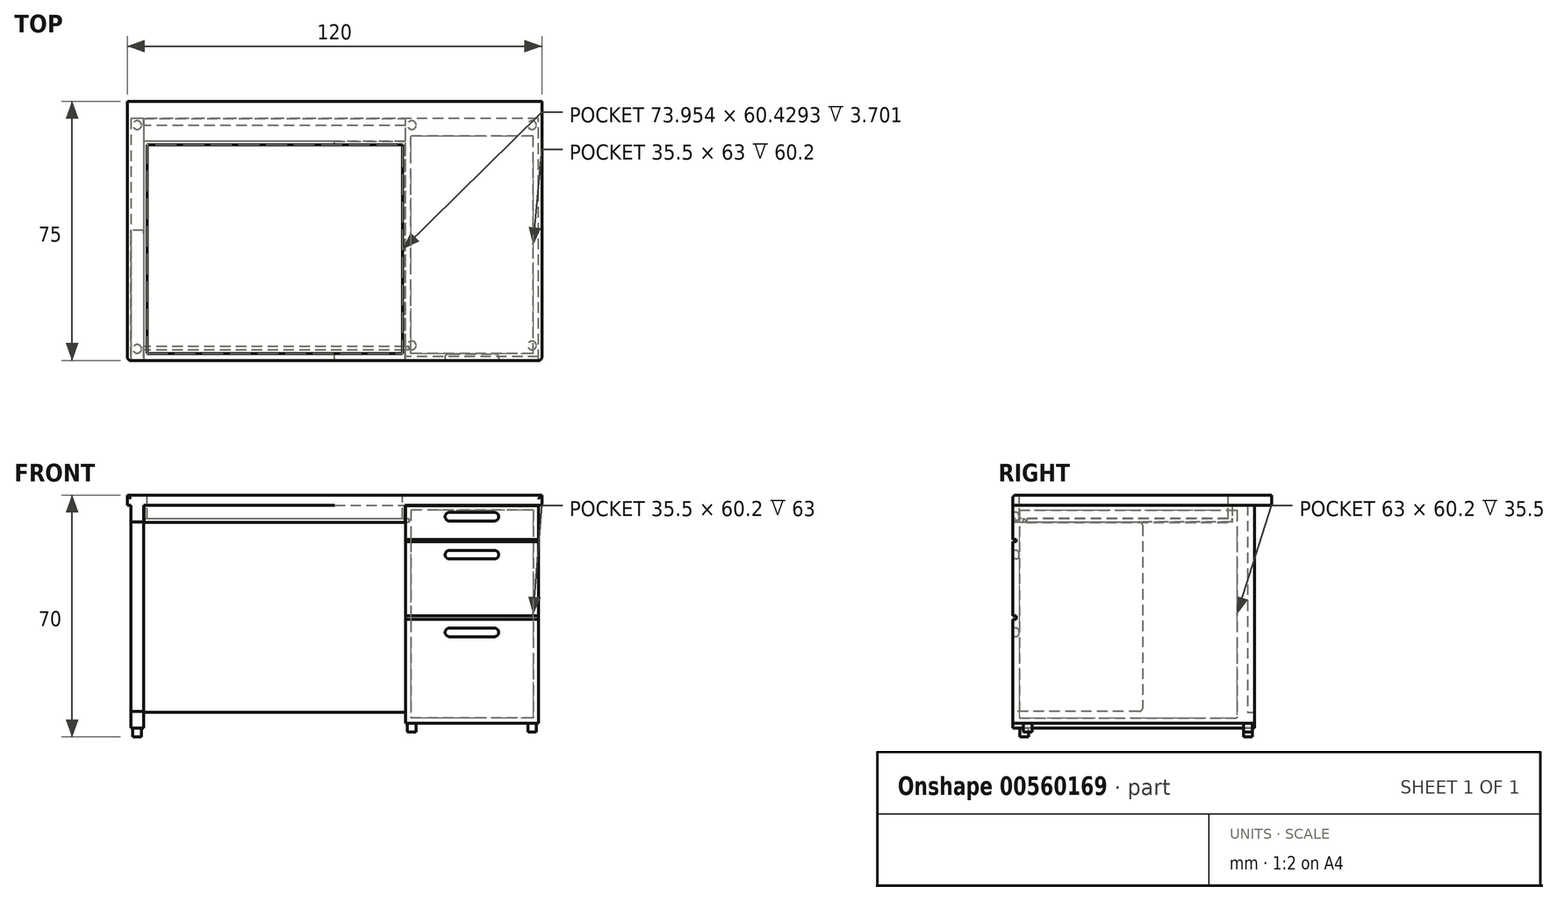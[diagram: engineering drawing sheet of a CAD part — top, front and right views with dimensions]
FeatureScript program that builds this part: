
annotation { "Feature Type Name" : "Feature", "Feature Type Description" : "" }
export const myFeature = defineFeature(function(context is Context, id is Id, definition is map)
    precondition{}
    {
        {
            var Q0;
            Q0=qCreatedBy(makeId("Top.planeOp"),FACE);
            var sketch = newSketch(context, id + "F0", { "sketchPlane" : qUnion([Q0])});
            skLineSegment(sketch, "E0.top", {"start": v(-60, -35) * mm, "end": v(60, -35) * mm});
            skPoint(sketch, "E0.middle", {"position": v(0, 0) * mm});
            skLineSegment(sketch, "E1", {"start": v(-60, 40) * mm, "end": v(60, 40) * mm});
            skLineSegment(sketch, "E2", {"start": v(-60, -35) * mm, "end": v(-60, 40) * mm});
            skLineSegment(sketch, "E3", {"start": v(60, 40) * mm, "end": v(60, -35) * mm});
            skSolve(sketch);
        }
        {
            var Q0;
            Q0 = qSketchRegion(id + "F0", true);
            extrude(context, id + "F1", {"entities" : qUnion([Q0]), "depth" : 2.9 * mm, "offsetDistance" : 25 * mm});
        }
        {
            var Q0;
            Q0=makeQuery(id+"F1.opExtrude","CAP_EDGE",EDGE,{"disambiguationData":[OSD([sQuery(id+"F0.wireOp",EDGE,"E0.bottom")])],"isStart":false});
            var Q1;
            Q1=makeQuery(id+"F1.opExtrude","CAP_EDGE",EDGE,{"disambiguationData":[OSD([sQuery(id+"F0.wireOp",EDGE,"E0.right")])],"isStart":false});
            var Q2;
            Q2=makeQuery(id+"F1.opExtrude","CAP_EDGE",EDGE,{"disambiguationData":[OSD([sQuery(id+"F0.wireOp",EDGE,"E0.left")])],"isStart":false});
            var Q3;
            Q3=makeQuery(id+"F1.opExtrude","CAP_EDGE",EDGE,{"disambiguationData":[OSD([sQuery(id+"F0.wireOp",EDGE,"E0.top")])],"isStart":false});
            var Q4;
            Q4=makeQuery(id+"F1.opExtrude","SWEPT_EDGE",EDGE,{"disambiguationData":[OSD([sQuery(id+"F0.wireOp",EDGE,"E0.top"),sQuery(id+"F0.wireOp",EDGE,"E0.left")])]});
            var Q5;
            Q5=makeQuery(id+"F1.opExtrude","SWEPT_EDGE",EDGE,{"disambiguationData":[OSD([sQuery(id+"F0.wireOp",EDGE,"E0.bottom"),sQuery(id+"F0.wireOp",EDGE,"E0.left")])]});
            var Q6;
            Q6=makeQuery(id+"F1.opExtrude","SWEPT_EDGE",EDGE,{"disambiguationData":[OSD([sQuery(id+"F0.wireOp",EDGE,"E0.bottom"),sQuery(id+"F0.wireOp",EDGE,"E0.right")])]});
            var Q7;
            Q7=makeQuery(id+"F1.opExtrude","SWEPT_EDGE",EDGE,{"disambiguationData":[OSD([sQuery(id+"F0.wireOp",EDGE,"E0.top"),sQuery(id+"F0.wireOp",EDGE,"E0.right")])]});
            fillet(context, id + "F2", {"entities" : qUnion([Q0, Q1, Q2, Q3, Q4, Q5, Q6, Q7]), "radius" : 1 * mm, "tangentPropagation" : true, "allowEdgeOverflow" : false});
        }
        {
            var Q0;
            Q0=qCreatedBy(makeId("Top.planeOp"),FACE);
            var sketch = newSketch(context, id + "F3", { "sketchPlane" : qUnion([Q0])});
            skLineSegment(sketch, "E4", {"start": v(-55.3, 0) * mm, "end": v(-55.3, -35) * mm});
            skLineSegment(sketch, "E5", {"start": v(-55.3, 0) * mm, "end": v(-55.3, 35) * mm});
            skLineSegment(sketch, "E6", {"start": v(-55.3, 35) * mm, "end": v(-59, 35) * mm});
            skLineSegment(sketch, "E7", {"start": v(-59, 35) * mm, "end": v(-59, -35) * mm});
            skLineSegment(sketch, "E8", {"start": v(-59, -35) * mm, "end": v(-55.3, -35) * mm});
            skPoint(sketch, "E9", {"position": v(-59, 0) * mm});
            skSolve(sketch);
        }
        {
            var Q0;
            Q0 = qSketchRegion(id + "F3", true);
            extrude(context, id + "F4", {"entities" : qUnion([Q0]), "operationType" : NewBodyOperationType.ADD, "oppositeDirection" : true, "depth" : 64.6 * mm, "offsetDistance" : 25 * mm});
        }
        {
            var Q0;
            Q0=qCreatedBy(makeId("Front.planeOp"),FACE);
            cPlane(context, id + "F5", {"entities" : qUnion([Q0]), "cplaneType" : CPlaneType.OFFSET, "offset" : 35 * mm, "oppositeDirection" : true, "width" : 150 * mm, "height" : 150 * mm});
        }
        {
            var Q0;
            Q0=qCreatedBy(id+"F5.planeOp",FACE);
            var sketch = newSketch(context, id + "F6", { "sketchPlane" : qUnion([Q0])});
            skLineSegment(sketch, "E10", {"start": v(0, 0) * mm, "end": v(-55.3, 0) * mm});
            skLineSegment(sketch, "E11.bottom", {"start": v(-55.3, 0) * mm, "end": v(20.5, 0) * mm});
            skLineSegment(sketch, "E11.top", {"start": v(-55.3, -60) * mm, "end": v(20.5, -60) * mm});
            skLineSegment(sketch, "E11.left", {"start": v(-55.3, 0) * mm, "end": v(-55.3, -60) * mm});
            skLineSegment(sketch, "E11.right", {"start": v(20.5, 0) * mm, "end": v(20.5, -60) * mm});
            skSolve(sketch);
        }
        {
            var Q0;
            Q0 = qSketchRegion(id + "F6", true);
            extrude(context, id + "F7", {"entities" : qUnion([Q0]), "operationType" : NewBodyOperationType.ADD, "depth" : 2 * mm, "offsetDistance" : 25 * mm});
        }
        {
            var Q0;
            Q0=makeQuery(id+"F7.boolean.opBoolean","MERGE",FACE,{"derivedFrom":[makeQuery(id+"F4.boolean.opBoolean","MERGE",FACE,{"derivedFrom":[makeQuery(id+"F1.opExtrude","SWEPT_FACE",FACE,{"disambiguationData":[OSD([sQuery(id+"F0.wireOp",EDGE,"E0.bottom")])]}),makeQuery(id+"F4.opExtrude","SWEPT_FACE",FACE,{"disambiguationData":[OSD([sQuery(id+"F3.wireOp",EDGE,"E6")])]})]}),makeQuery(id+"F7.opExtrude","CAP_FACE",FACE,{"disambiguationData":[OSD([sQuery(id+"F6.wireOp",EDGE,"E11.bottom"),sQuery(id+"F6.wireOp",EDGE,"E11.top"),sQuery(id+"F6.wireOp",EDGE,"E11.left"),sQuery(id+"F6.wireOp",EDGE,"E11.right")])],"isStart":true})]});
            var sketch = newSketch(context, id + "F8", { "sketchPlane" : qUnion([Q0])});
            skLineSegment(sketch, "E12", {"start": v(-20.5, 0) * mm, "end": v(-20.5, -9.9) * mm});
            skLineSegment(sketch, "E13", {"start": v(-20.5, -9.9) * mm, "end": v(-20.5, -31.4) * mm});
            skLineSegment(sketch, "E14", {"start": v(-20.5, -31.4) * mm, "end": v(-20.5, -63.2) * mm});
            skLineSegment(sketch, "E15.bottom", {"start": v(-20.5, 0) * mm, "end": v(-59, 0) * mm});
            skLineSegment(sketch, "E15.right", {"start": v(-59, 0) * mm, "end": v(-59, -9.9) * mm});
            skLineSegment(sketch, "E16.left", {"start": v(-59, -9.9) * mm, "end": v(-59, -31.4) * mm});
            skLineSegment(sketch, "E17.top", {"start": v(-59, -63.2) * mm, "end": v(-20.5, -63.2) * mm});
            skLineSegment(sketch, "E17.left", {"start": v(-59, -31.4) * mm, "end": v(-59, -63.2) * mm});
            skLineSegment(sketch, "E18.bottom", {"start": v(-57.5, -1.5) * mm, "end": v(-22, -1.5) * mm});
            skLineSegment(sketch, "E18.top", {"start": v(-57.5, -61.7) * mm, "end": v(-22, -61.7) * mm});
            skLineSegment(sketch, "E18.left", {"start": v(-57.5, -1.5) * mm, "end": v(-57.5, -61.7) * mm});
            skLineSegment(sketch, "E18.right", {"start": v(-22, -1.5) * mm, "end": v(-22, -61.7) * mm});
            skSolve(sketch);
        }
        {
            var Q0;
            Q0=makeQuery(id+"F4.opExtrude","SWEPT_FACE",FACE,{"disambiguationData":[OSD([sQuery(id+"F3.wireOp",EDGE,"E7")])]});
            var sketch = newSketch(context, id + "F9", { "sketchPlane" : qUnion([Q0])});
            skLineSegment(sketch, "E19", {"start": v(35, -4.9) * mm, "end": v(-2.66, -4.9) * mm});
            skLineSegment(sketch, "E20", {"start": v(-2.66, -4.9) * mm, "end": v(-2.66, -59.7) * mm});
            skLineSegment(sketch, "E21", {"start": v(-2.66, -59.7) * mm, "end": v(35, -59.7) * mm});
            skLineSegment(sketch, "E22", {"start": v(35, -59.7) * mm, "end": v(35, -4.9) * mm});
            skSolve(sketch);
        }
        {
            var Q0;
            Q0 = qSketchRegion(id + "F9", true);
            extrude(context, id + "F10", {"entities" : qUnion([Q0]), "operationType" : NewBodyOperationType.REMOVE, "oppositeDirection" : true, "depth" : 25 * mm, "offsetDistance" : 25 * mm});
        }
        {
            var Q0;
            Q0=makeQuery(id+"F10.boolean.opBoolean","COPY",EDGE,{"derivedFrom":makeQuery(id+"F10.opExtrude","SWEPT_EDGE",EDGE,{"disambiguationData":[OSD([sQuery(id+"F9.wireOp",EDGE,"E19"),sQuery(id+"F9.wireOp",EDGE,"E20")])]})});
            var Q1;
            Q1=makeQuery(id+"F10.boolean.opBoolean","COPY",EDGE,{"derivedFrom":makeQuery(id+"F10.opExtrude","SWEPT_EDGE",EDGE,{"disambiguationData":[OSD([sQuery(id+"F9.wireOp",EDGE,"E20"),sQuery(id+"F9.wireOp",EDGE,"E21")])]})});
            var Q2;
            Q2=makeQuery(id+"F10.boolean.opBoolean","COPY",EDGE,{"derivedFrom":makeQuery(id+"F10.opExtrude","SWEPT_EDGE",EDGE,{"disambiguationData":[OSD([sQuery(id+"F3.wireOp",EDGE,"E7"),sQuery(id+"F3.wireOp",EDGE,"E8"),sQuery(id+"F9.wireOp",EDGE,"E19"),sQuery(id+"F9.wireOp",EDGE,"E22")])]})});
            var Q3;
            Q3=makeQuery(id+"F10.boolean.opBoolean","COPY",EDGE,{"derivedFrom":makeQuery(id+"F10.opExtrude","SWEPT_EDGE",EDGE,{"disambiguationData":[OSD([sQuery(id+"F3.wireOp",EDGE,"E7"),sQuery(id+"F3.wireOp",EDGE,"E8"),sQuery(id+"F9.wireOp",EDGE,"E21"),sQuery(id+"F9.wireOp",EDGE,"E22")])]})});
            fillet(context, id + "F11", {"entities" : qUnion([Q0, Q1, Q2, Q3]), "radius" : 1 * mm, "tangentPropagation" : true, "allowEdgeOverflow" : false});
        }
        {
            var Q0;
            Q0 = qSketchRegion(id + "F8", true);
            extrude(context, id + "F12", {"entities" : qUnion([Q0]), "operationType" : NewBodyOperationType.ADD, "oppositeDirection" : true, "depth" : 68 * mm, "offsetDistance" : 25 * mm});
        }
        {
            var Q0;
            Q0=makeQuery(id+"F12.boolean.opBoolean","MERGE",FACE,{"derivedFrom":[makeQuery(id+"F7.boolean.opBoolean","MERGE",FACE,{"derivedFrom":[makeQuery(id+"F4.boolean.opBoolean","MERGE",FACE,{"derivedFrom":[makeQuery(id+"F1.opExtrude","SWEPT_FACE",FACE,{"disambiguationData":[OSD([sQuery(id+"F0.wireOp",EDGE,"E0.bottom")])]}),makeQuery(id+"F4.opExtrude","SWEPT_FACE",FACE,{"disambiguationData":[OSD([sQuery(id+"F3.wireOp",EDGE,"E6")])]})]}),makeQuery(id+"F7.opExtrude","CAP_FACE",FACE,{"disambiguationData":[OSD([sQuery(id+"F6.wireOp",EDGE,"E11.bottom"),sQuery(id+"F6.wireOp",EDGE,"E11.top"),sQuery(id+"F6.wireOp",EDGE,"E11.left"),sQuery(id+"F6.wireOp",EDGE,"E11.right")])],"isStart":true})]}),makeQuery(id+"F12.opExtrude","CAP_FACE",FACE,{"disambiguationData":[OSD([sQuery(id+"F8.wireOp",EDGE,"E15.bottom"),sQuery(id+"F8.wireOp",EDGE,"E12"),sQuery(id+"F8.wireOp",EDGE,"E15.right"),sQuery(id+"F8.wireOp",EDGE,"E16.left"),sQuery(id+"F8.wireOp",EDGE,"E13"),sQuery(id+"F8.wireOp",EDGE,"E17.top"),sQuery(id+"F8.wireOp",EDGE,"E17.left"),sQuery(id+"F8.wireOp",EDGE,"E14"),sQuery(id+"F8.wireOp",EDGE,"E18.bottom"),sQuery(id+"F8.wireOp",EDGE,"E18.top"),sQuery(id+"F8.wireOp",EDGE,"E18.left"),sQuery(id+"F8.wireOp",EDGE,"E18.right")])],"isStart":true})]});
            var sketch = newSketch(context, id + "F13", { "sketchPlane" : qUnion([Q0])});
            skLineSegment(sketch, "E23.bottom", {"start": v(-57.5, -1.5) * mm, "end": v(-22, -1.5) * mm});
            skLineSegment(sketch, "E23.top", {"start": v(-57.5, -61.7) * mm, "end": v(-22, -61.7) * mm});
            skLineSegment(sketch, "E23.left", {"start": v(-57.5, -1.5) * mm, "end": v(-57.5, -61.7) * mm});
            skLineSegment(sketch, "E23.right", {"start": v(-22, -1.5) * mm, "end": v(-22, -61.7) * mm});
            skSolve(sketch);
        }
        {
            var Q0;
            Q0 = qSketchRegion(id + "F13", true);
            extrude(context, id + "F14", {"entities" : qUnion([Q0]), "operationType" : NewBodyOperationType.ADD, "oppositeDirection" : true, "depth" : 5 * mm, "offsetDistance" : 25 * mm});
        }
        {
            var Q0;
            Q0=qCreatedBy(makeId("Front.planeOp"),FACE);
            cPlane(context, id + "F15", {"entities" : qUnion([Q0]), "cplaneType" : CPlaneType.OFFSET, "offset" : 28.5 * mm, "oppositeDirection" : true, "width" : 150 * mm, "height" : 150 * mm});
        }
        {
            var Q0;
            Q0=qCreatedBy(id+"F15.planeOp",FACE);
            var sketch = newSketch(context, id + "F16", { "sketchPlane" : qUnion([Q0])});
            skLineSegment(sketch, "E24", {"start": v(0, 0) * mm, "end": v(20.5, 0) * mm});
            skLineSegment(sketch, "E25", {"start": v(20.5, 0) * mm, "end": v(20.5, -0.1) * mm});
            skLineSegment(sketch, "E26", {"start": v(0, 0) * mm, "end": v(-55, -0.1) * mm});
            skLineSegment(sketch, "E27", {"start": v(20.5, -0.1) * mm, "end": v(20.4, -0.1) * mm});
            skLineSegment(sketch, "E28.bottom", {"start": v(20.4, -0.1) * mm, "end": v(-55.2, -0.1) * mm});
            skLineSegment(sketch, "E28.top", {"start": v(20.4, -5) * mm, "end": v(-55.2, -5) * mm});
            skLineSegment(sketch, "E28.left", {"start": v(20.4, -0.1) * mm, "end": v(20.4, -5) * mm});
            skLineSegment(sketch, "E28.right", {"start": v(-55.2, -0.1) * mm, "end": v(-55.2, -5) * mm});
            skSolve(sketch);
        }
        {
            var Q0;
            Q0 = qSketchRegion(id + "F16", true);
            extrude(context, id + "F17", {"entities" : qUnion([Q0]), "depth" : 63.5 * mm, "offsetDistance" : 25 * mm});
        }
        {
            var Q0;
            Q0=makeQuery(id+"F17.opExtrude","CAP_EDGE",EDGE,{"disambiguationData":[OSD([sQuery(id+"F16.wireOp",EDGE,"E28.top")])],"isStart":false});
            fillet(context, id + "F18", {"entities" : qUnion([Q0]), "radius" : 3 * mm, "tangentPropagation" : true, "allowEdgeOverflow" : false});
        }
        {
            var Q0;
            Q0=makeQuery(id+"F17.opExtrude","SWEPT_FACE",FACE,{"disambiguationData":[OSD([sQuery(id+"F16.wireOp",EDGE,"E28.right")])]});
            var sketch = newSketch(context, id + "F19", { "sketchPlane" : qUnion([Q0])});
            skLineSegment(sketch, "E29", {"start": v(32, -5) * mm, "end": v(32, -4) * mm});
            skLineSegment(sketch, "E30", {"start": v(32, -5) * mm, "end": v(31, -5) * mm});
            skArc(sketch, "E31", {"start": v(32, -4) * mm, "mid": v(31.3, -4.3) * mm, "end": v(31, -5) * mm});
            skSolve(sketch);
        }
        {
            var Q0;
            Q0 = qSketchRegion(id + "F19", true);
            extrude(context, id + "F20", {"entities" : qUnion([Q0]), "operationType" : NewBodyOperationType.REMOVE, "oppositeDirection" : true, "depth" : 76.8 * mm, "offsetDistance" : 25 * mm});
        }
        {
            var Q0;
            Q0=makeQuery(id+"F1.opExtrude","CAP_FACE",FACE,{"disambiguationData":[OSD([sQuery(id+"F0.wireOp",EDGE,"E0.bottom"),sQuery(id+"F0.wireOp",EDGE,"E0.top"),sQuery(id+"F0.wireOp",EDGE,"E0.left"),sQuery(id+"F0.wireOp",EDGE,"E0.right")])],"isStart":false});
            var sketch = newSketch(context, id + "F21", { "sketchPlane" : qUnion([Q0])});
            skLineSegment(sketch, "E32.bottom", {"start": v(-54.3, 27.43) * mm, "end": v(19.66, 27.43) * mm});
            skLineSegment(sketch, "E32.top", {"start": v(-54.3, -33) * mm, "end": v(19.66, -33) * mm});
            skLineSegment(sketch, "E32.left", {"start": v(-54.3, 27.43) * mm, "end": v(-54.3, -33) * mm});
            skLineSegment(sketch, "E32.right", {"start": v(19.66, 27.43) * mm, "end": v(19.66, -33) * mm});
            skSolve(sketch);
        }
        {
            var Q0;
            Q0 = qSketchRegion(id + "F21", true);
            extrude(context, id + "F22", {"entities" : qUnion([Q0]), "operationType" : NewBodyOperationType.REMOVE, "oppositeDirection" : true, "depth" : 6.7 * mm, "offsetDistance" : 25 * mm});
        }
        {
            var Q0;
            Q0=makeQuery(id+"F4.opExtrude","CAP_FACE",FACE,{"disambiguationData":[OSD([sQuery(id+"F3.wireOp",EDGE,"E4"),sQuery(id+"F3.wireOp",EDGE,"E5"),sQuery(id+"F3.wireOp",EDGE,"E6"),sQuery(id+"F3.wireOp",EDGE,"E7"),sQuery(id+"F3.wireOp",EDGE,"E8")])],"isStart":false});
            var sketch = newSketch(context, id + "F23", { "sketchPlane" : qUnion([Q0])});
            skCircle(sketch, "E33", {"center": v(-57.15, 33.15) * mm, "radius": 1.25 * mm});
            skCircle(sketch, "E34", {"center": v(-57.15, -33.15) * mm, "radius": 1.25 * mm});
            skSolve(sketch);
        }
        {
            var Q0;
            Q0=makeQuery(id+"F12.opExtrude","SWEPT_FACE",FACE,{"disambiguationData":[OSD([sQuery(id+"F8.wireOp",EDGE,"E17.top")])]});
            var sketch = newSketch(context, id + "F24", { "sketchPlane" : qUnion([Q0])});
            skCircle(sketch, "E35", {"center": v(22.35, 98.45) * mm, "radius": 1.25 * mm});
            skCircle(sketch, "E36", {"center": v(22.35, 32.15) * mm, "radius": 1.25 * mm});
            skCircle(sketch, "E37", {"center": v(57.15, 98.45) * mm, "radius": 1.25 * mm});
            skCircle(sketch, "E38", {"center": v(57.15, 32.15) * mm, "radius": 1.25 * mm});
            skCircle(sketch, "E39", {"center": v(22.35, -33.15) * mm, "radius": 1.25 * mm});
            skCircle(sketch, "E40", {"center": v(57.15, -33.15) * mm, "radius": 1.25 * mm});
            skSolve(sketch);
        }
        {
            var Q0;
            Q0 = qSketchRegion(id + "F23", true);
            extrude(context, id + "F25", {"entities" : qUnion([Q0]), "depth" : 2.5 * mm, "offsetDistance" : 25 * mm});
        }
        {
            var Q0;
            Q0 = qSketchRegion(id + "F24", true);
            extrude(context, id + "F26", {"entities" : qUnion([Q0]), "depth" : 2.5 * mm, "offsetDistance" : 25 * mm});
        }
        {
            var Q0;
            Q0=makeQuery(id+"F26.opExtrude","SWEPT_BODY",BODY,{"disambiguationData":[OSD([sQuery(id+"F24.wireOp",EDGE,"E35")])]});
            var Q1;
            Q1=makeQuery(id+"F26.opExtrude","SWEPT_BODY",BODY,{"disambiguationData":[OSD([sQuery(id+"F24.wireOp",EDGE,"E37")])]});
            deleteBodies(context, id + "F27", {"entities" : qUnion([Q0, Q1])});
        }
        {
            var Q0;
            Q0=makeQuery(id+"F25.opExtrude","SWEPT_BODY",BODY,{"disambiguationData":[OSD([sQuery(id+"F23.wireOp",EDGE,"E33")])]});
            var Q1;
            Q1=makeQuery(id+"F26.opExtrude","SWEPT_BODY",BODY,{"disambiguationData":[OSD([sQuery(id+"F24.wireOp",EDGE,"E36")])]});
            var Q2;
            Q2=makeQuery(id+"F26.opExtrude","SWEPT_BODY",BODY,{"disambiguationData":[OSD([sQuery(id+"F24.wireOp",EDGE,"E38")])]});
            transform(context, id + "F28", {"entities" : qUnion([Q0, Q1, Q2]), "transformType" : TransformType.TRANSLATION_3D, "dx" : 0 * mm, "dy" : 1.5 * mm, "dz" : 0 * mm, "makeCopy" : false});
        }
        {
            var Q0;
            Q0=makeQuery(id+"F4.opExtrude","SWEPT_FACE",FACE,{"disambiguationData":[OSD([sQuery(id+"F3.wireOp",EDGE,"E7")])]});
            var sketch = newSketch(context, id + "F29", { "sketchPlane" : qUnion([Q0])});
            skLineSegment(sketch, "E41.bottom", {"start": v(-28.5, -3.84) * mm, "end": v(30.78, -3.84) * mm});
            skLineSegment(sketch, "E41.top", {"start": v(-28.5, -4.9) * mm, "end": v(30.78, -4.9) * mm});
            skLineSegment(sketch, "E41.left", {"start": v(-28.5, -3.84) * mm, "end": v(-28.5, -4.9) * mm});
            skLineSegment(sketch, "E41.right", {"start": v(30.78, -3.84) * mm, "end": v(30.78, -4.9) * mm});
            skSolve(sketch);
        }
        {
            var Q0;
            Q0 = qSketchRegion(id + "F29", true);
            extrude(context, id + "F30", {"entities" : qUnion([Q0]), "operationType" : NewBodyOperationType.ADD, "oppositeDirection" : true, "depth" : 80.92 * mm, "offsetDistance" : 25 * mm});
        }
        {
            var Q0;
            Q0=makeQuery(id+"F12.opExtrude","CAP_FACE",FACE,{"disambiguationData":[OSD([sQuery(id+"F8.wireOp",EDGE,"E15.bottom"),sQuery(id+"F8.wireOp",EDGE,"E12"),sQuery(id+"F8.wireOp",EDGE,"E15.right"),sQuery(id+"F8.wireOp",EDGE,"E16.left"),sQuery(id+"F8.wireOp",EDGE,"E13"),sQuery(id+"F8.wireOp",EDGE,"E17.top"),sQuery(id+"F8.wireOp",EDGE,"E17.left"),sQuery(id+"F8.wireOp",EDGE,"E14"),sQuery(id+"F8.wireOp",EDGE,"E18.bottom"),sQuery(id+"F8.wireOp",EDGE,"E18.top"),sQuery(id+"F8.wireOp",EDGE,"E18.left"),sQuery(id+"F8.wireOp",EDGE,"E18.right")])],"isStart":false});
            var sketch = newSketch(context, id + "F31", { "sketchPlane" : qUnion([Q0])});
            skLineSegment(sketch, "E42.bottom", {"start": v(20.5, 0) * mm, "end": v(59, 0) * mm});
            skLineSegment(sketch, "E42.top", {"start": v(20.5, -9.9) * mm, "end": v(59, -9.9) * mm});
            skLineSegment(sketch, "E42.left", {"start": v(20.5, 0) * mm, "end": v(20.5, -9.9) * mm});
            skLineSegment(sketch, "E42.right", {"start": v(59, 0) * mm, "end": v(59, -9.9) * mm});
            skLineSegment(sketch, "E43.bottom", {"start": v(20.5, -10.6) * mm, "end": v(59, -10.6) * mm});
            skLineSegment(sketch, "E43.top", {"start": v(20.5, -32.1) * mm, "end": v(59, -32.1) * mm});
            skLineSegment(sketch, "E43.left", {"start": v(20.5, -10.6) * mm, "end": v(20.5, -32.1) * mm});
            skLineSegment(sketch, "E43.right", {"start": v(59, -10.6) * mm, "end": v(59, -32.1) * mm});
            skLineSegment(sketch, "E44.bottom", {"start": v(20.5, -33.07) * mm, "end": v(59, -33.07) * mm});
            skLineSegment(sketch, "E44.top", {"start": v(20.5, -63.2) * mm, "end": v(59, -63.2) * mm});
            skLineSegment(sketch, "E44.left", {"start": v(20.5, -33.07) * mm, "end": v(20.5, -63.2) * mm});
            skLineSegment(sketch, "E44.right", {"start": v(59, -33.07) * mm, "end": v(59, -63.2) * mm});
            skSolve(sketch);
        }
        {
            var Q0;
            Q0 = qSketchRegion(id + "F31", true);
            extrude(context, id + "F32", {"entities" : qUnion([Q0]), "operationType" : NewBodyOperationType.ADD, "depth" : 2 * mm, "offsetDistance" : 25 * mm});
        }
        {
            var Q0;
            Q0=makeQuery(id+"F1.opExtrude","CAP_FACE",FACE,{"disambiguationData":[OSD([sQuery(id+"F0.wireOp",EDGE,"E0.top"),sQuery(id+"F0.wireOp",EDGE,"E1"),sQuery(id+"F0.wireOp",EDGE,"E2"),sQuery(id+"F0.wireOp",EDGE,"E3")])],"isStart":true});
            var sketch = newSketch(context, id + "F33", { "sketchPlane" : qUnion([Q0])});
            skLineSegment(sketch, "E45.bottom", {"start": v(59, 33) * mm, "end": v(20.5, 33) * mm});
            skLineSegment(sketch, "E45.top", {"start": v(59, 33.9) * mm, "end": v(20.5, 33.9) * mm});
            skLineSegment(sketch, "E45.left", {"start": v(59, 33) * mm, "end": v(59, 33.9) * mm});
            skLineSegment(sketch, "E45.right", {"start": v(20.5, 33) * mm, "end": v(20.5, 33.9) * mm});
            skSolve(sketch);
        }
        {
            var Q0;
            Q0 = qSketchRegion(id + "F33", true);
            extrude(context, id + "F34", {"entities" : qUnion([Q0]), "operationType" : NewBodyOperationType.ADD, "depth" : 62.82 * mm, "offsetDistance" : 25 * mm});
        }
        {
            var Q0;
            {var subQ0=sQuery(id+"F0.wireOp",EDGE,"E0.top");Q0=makeQuery(id+"F32.boolean.opBoolean","MERGE",FACE,{"derivedFrom":[makeQuery(id+"F10.boolean.opBoolean","SPLIT",FACE,{"disambiguationData":[TD([makeQuery(id+"F2.opFillet","BLEND_FACE",FACE,{"disambiguationData":[OSD([subQ0])]})])],"derivedFrom":makeQuery(id+"F4.boolean.opBoolean","MERGE",FACE,{"derivedFrom":[makeQuery(id+"F1.opExtrude","SWEPT_FACE",FACE,{"disambiguationData":[OSD([subQ0])]}),makeQuery(id+"F4.opExtrude","SWEPT_FACE",FACE,{"disambiguationData":[OSD([sQuery(id+"F3.wireOp",EDGE,"E8")])]})]})}),makeQuery(id+"F32.opExtrude","CAP_FACE",FACE,{"disambiguationData":[OSD([sQuery(id+"F31.wireOp",EDGE,"E42.bottom"),sQuery(id+"F31.wireOp",EDGE,"E42.top"),sQuery(id+"F31.wireOp",EDGE,"E42.left"),sQuery(id+"F31.wireOp",EDGE,"E42.right")])],"isStart":false})]});}
            var sketch = newSketch(context, id + "F35", { "sketchPlane" : qUnion([Q0])});
            skLineSegment(sketch, "E46.bottom", {"start": v(59, 0) * mm, "end": v(20.5, 0) * mm});
            skLineSegment(sketch, "E46.top", {"start": v(59, -0.12) * mm, "end": v(20.5, -0.12) * mm});
            skLineSegment(sketch, "E46.left", {"start": v(59, 0) * mm, "end": v(59, -0.12) * mm});
            skLineSegment(sketch, "E46.right", {"start": v(20.5, 0) * mm, "end": v(20.5, -0.12) * mm});
            skSolve(sketch);
        }
        {
            var Q0;
            Q0 = qSketchRegion(id + "F35", true);
            extrude(context, id + "F36", {"entities" : qUnion([Q0]), "operationType" : NewBodyOperationType.REMOVE, "oppositeDirection" : true, "depth" : 0.1 * mm, "offsetDistance" : 25 * mm});
        }
        {
            var Q0;
            {var subQ0=sQuery(id+"F31.wireOp",EDGE,"E42.right");var subQ1=sQuery(id+"F31.wireOp",EDGE,"E42.top");var subQ2=sQuery(id+"F31.wireOp",EDGE,"E42.left");var subQ3=sQuery(id+"F0.wireOp",EDGE,"E0.top");Q0=makeQuery(id+"F36.boolean.opBoolean","SPLIT",FACE,{"disambiguationData":[TD([makeQuery(id+"F32.opExtrude","SWEPT_FACE",FACE,{"disambiguationData":[OSD([subQ1])]})])],"derivedFrom":makeQuery(id+"F32.boolean.opBoolean","MERGE",FACE,{"derivedFrom":[makeQuery(id+"F10.boolean.opBoolean","SPLIT",FACE,{"disambiguationData":[TD([makeQuery(id+"F2.opFillet","BLEND_FACE",FACE,{"disambiguationData":[OSD([subQ3])]})])],"derivedFrom":makeQuery(id+"F4.boolean.opBoolean","MERGE",FACE,{"derivedFrom":[makeQuery(id+"F1.opExtrude","SWEPT_FACE",FACE,{"disambiguationData":[OSD([subQ3])]}),makeQuery(id+"F4.opExtrude","SWEPT_FACE",FACE,{"disambiguationData":[OSD([sQuery(id+"F3.wireOp",EDGE,"E8")])]})]})}),makeQuery(id+"F32.opExtrude","CAP_FACE",FACE,{"disambiguationData":[OSD([sQuery(id+"F31.wireOp",EDGE,"E42.bottom"),subQ1,subQ2,subQ0])],"isStart":false})]})});}
            var sketch = newSketch(context, id + "F37", { "sketchPlane" : qUnion([Q0])});
            skPoint(sketch, "E47.endSnap0", {"position": v(39.75, -0.12) * mm});
            skLineSegment(sketch, "E48.bottom", {"start": v(33.25, -4.6) * mm, "end": v(46.25, -4.6) * mm});
            skLineSegment(sketch, "E48.top", {"start": v(33.25, -2.1) * mm, "end": v(46.25, -2.1) * mm});
            skPoint(sketch, "E48.middle", {"position": v(39.75, -3.35) * mm});
            skArc(sketch, "E49", {"start": v(46.25, -2.1) * mm, "mid": v(47.5, -3.35) * mm, "end": v(46.25, -4.6) * mm});
            skArc(sketch, "E50", {"start": v(33.25, -2.1) * mm, "mid": v(32, -3.35) * mm, "end": v(33.25, -4.6) * mm});
            skLineSegment(sketch, "E51.bottom", {"start": v(33.25, -15.6) * mm, "end": v(46.25, -15.6) * mm});
            skLineSegment(sketch, "E51.top", {"start": v(33.25, -13.1) * mm, "end": v(46.25, -13.1) * mm});
            skPoint(sketch, "E51.middle", {"position": v(39.75, -14.36) * mm});
            skArc(sketch, "E52", {"start": v(46.25, -13.1) * mm, "mid": v(47.5, -14.36) * mm, "end": v(46.25, -15.6) * mm});
            skArc(sketch, "E53", {"start": v(33.25, -13.1) * mm, "mid": v(32, -14.36) * mm, "end": v(33.25, -15.6) * mm});
            skLineSegment(sketch, "E54.bottom", {"start": v(33.25, -38.1) * mm, "end": v(46.25, -38.1) * mm});
            skLineSegment(sketch, "E54.top", {"start": v(33.25, -35.6) * mm, "end": v(46.25, -35.6) * mm});
            skPoint(sketch, "E54.middle", {"position": v(39.75, -36.86) * mm});
            skArc(sketch, "E55", {"start": v(46.25, -35.6) * mm, "mid": v(47.5, -36.86) * mm, "end": v(46.25, -38.1) * mm});
            skArc(sketch, "E56", {"start": v(33.25, -35.6) * mm, "mid": v(32, -36.86) * mm, "end": v(33.25, -38.1) * mm});
            skSolve(sketch);
        }
        {
            var Q0;
            Q0 = qSketchRegion(id + "F37", true);
            extrude(context, id + "F38", {"entities" : qUnion([Q0]), "operationType" : NewBodyOperationType.REMOVE, "oppositeDirection" : true, "depth" : 1.9 * mm, "offsetDistance" : 25 * mm});
        }
        {
            var Q0;
            Q0=makeQuery(id+"F38.boolean.opBoolean","COPY",FACE,{"derivedFrom":makeQuery(id+"F38.opExtrude","CAP_FACE",FACE,{"disambiguationData":[OSD([sQuery(id+"F37.wireOp",EDGE,"E48.bottom"),sQuery(id+"F37.wireOp",EDGE,"E48.top"),sQuery(id+"F37.wireOp",EDGE,"E49"),sQuery(id+"F37.wireOp",EDGE,"E50")])],"isStart":false})});
            var Q1;
            Q1=makeQuery(id+"F38.boolean.opBoolean","COPY",FACE,{"derivedFrom":makeQuery(id+"F38.opExtrude","CAP_FACE",FACE,{"disambiguationData":[OSD([sQuery(id+"F37.wireOp",EDGE,"E51.bottom"),sQuery(id+"F37.wireOp",EDGE,"E51.top"),sQuery(id+"F37.wireOp",EDGE,"E52"),sQuery(id+"F37.wireOp",EDGE,"E53")])],"isStart":false})});
            var Q2;
            Q2=makeQuery(id+"F38.boolean.opBoolean","COPY",FACE,{"derivedFrom":makeQuery(id+"F38.opExtrude","CAP_FACE",FACE,{"disambiguationData":[OSD([sQuery(id+"F37.wireOp",EDGE,"E54.bottom"),sQuery(id+"F37.wireOp",EDGE,"E54.top"),sQuery(id+"F37.wireOp",EDGE,"E55"),sQuery(id+"F37.wireOp",EDGE,"E56")])],"isStart":false})});
            fillet(context, id + "F39", {"entities" : qUnion([Q0, Q1, Q2]), "radius" : 1 * mm, "tangentPropagation" : true, "allowEdgeOverflow" : false});
        }
    });
